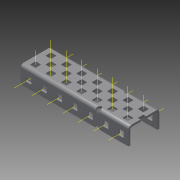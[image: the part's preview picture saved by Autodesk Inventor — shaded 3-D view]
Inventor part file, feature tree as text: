
AUTODESK INVENTOR PART (.ipt)
format: ipt  version: 2015 (Build 190159000, 159)  size: 1,973,760 bytes
history: native  units: in
note: dims shown in document units (in); Inventor stores cm internally (conversion verified against a paired STEP export)
features: other x42, pattern_linear x3, sheet_metal_op x1, extrude x1, imported_body x1, sketch x1
ambient origin geometry x8: Origin, YZ Plane, XZ Plane, XY Plane, X Axis, Y Axis, Z Axis, Center Point
bodies: Body1 (feature_tree)
feature tree (49):
  other  "C-Channel 2 x 7 (aluminum)"
  sheet_metal_op  "Fold1"
  other  "C-Channel"
  extrude  "length cut"  Depth=0.5in
  other  "top axis"
  other  "inner axis"
  other  "front axis"
  other  "back axis"
  pattern_linear  "top axes"  Spacing1=0.5in  [1 undecoded]
  pattern_linear  "inner axes"  Spacing1=0.5in  [1 undecoded]
  pattern_linear  "horiz axes"  Spacing1=-3.5in  [1 undecoded]
  other  "right plane"
  imported_body  "Base1"
  sketch  "Sketch1"  dims[d1=0.0in d4=0.5in d5=0.7874in d7=0.5in d10=0.5in d13=0.5in d14=-3.5in d15=0.0in d16=0.0in d17=0.0in d18=0.0in d19=0.0in]
  other  "Work Point1"
  other  "Work Point2"
  other  "Work Point3"
  other  "Work Point4"
  other  "Work Axis5"
  other  "Work Axis6"
  other  "Work Axis7"
  other  "Work Axis8"
  other  "Work Axis11"
  other  "Work Axis12"
  other  "Work Axis13"
  other  "Work Axis14"
  other  "Work Axis15"
  other  "Work Axis18"
  other  "Work Axis19"
  other  "Work Axis20"
  other  "Work Axis23"
  other  "Work Axis24"
  other  "Work Axis25"
  other  "Work Axis26"
  other  "Work Axis30"
  other  "Work Axis31"
  other  "Work Axis32"
  other  "Work Axis33"
  other  "left plane"
  other  "Work Axis137"
  other  "Work Axis138"
  other  "Work Axis142"
  other  "Work Axis143"
  other  "Work Axis147"
  other  "Work Axis148"
  other  "Work Axis152"
  other  "Work Axis153"
  other  "Work Axis157"
  other  "Work Axis158"
note: 3 required parameter values undecoded (feature->parameter linkage not recoverable at this tier; creation-order binding heuristic only, values carry confidence <= 0.55)
